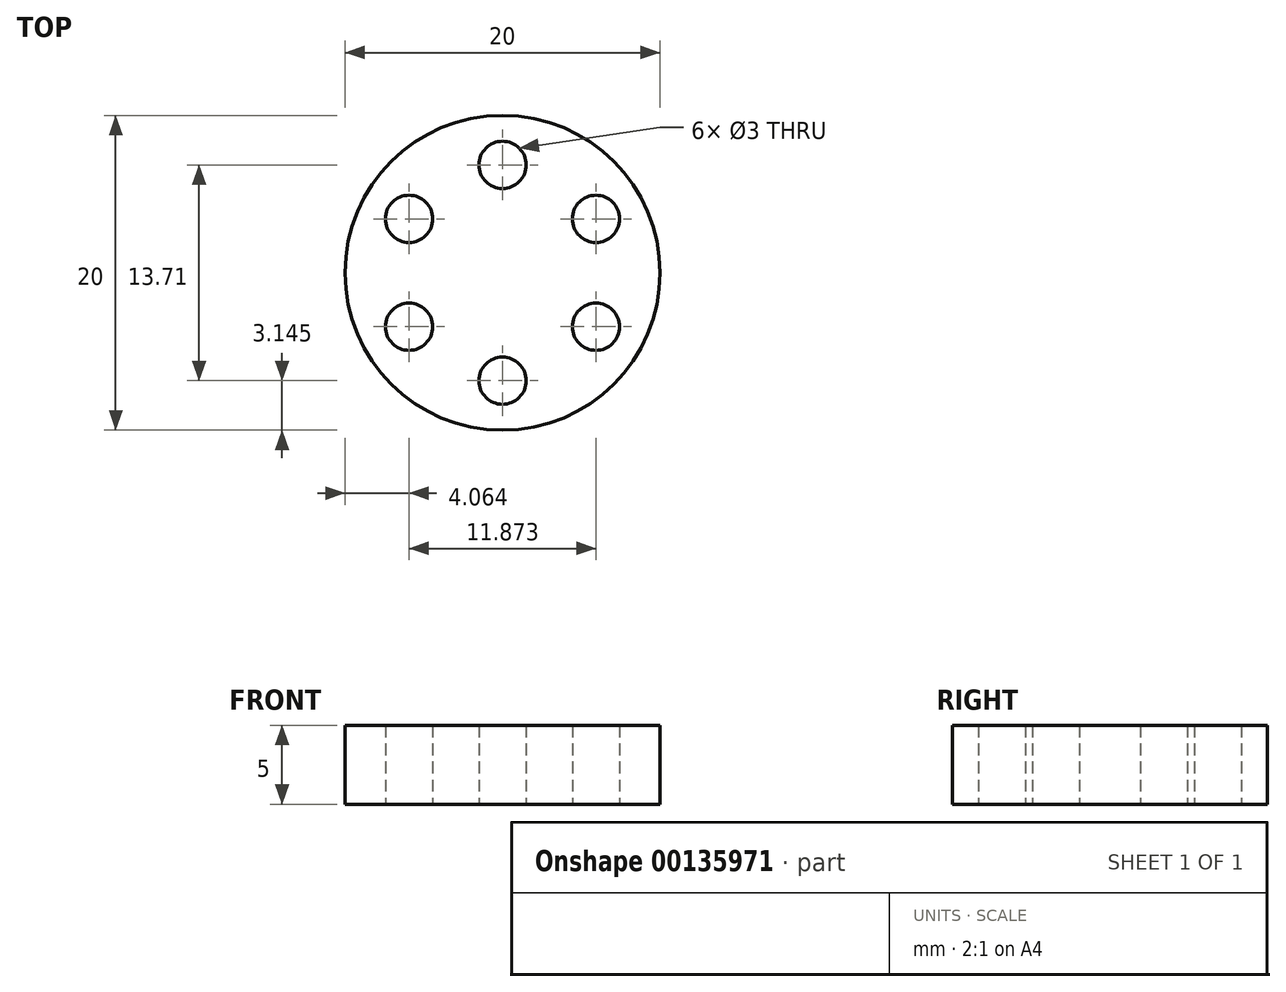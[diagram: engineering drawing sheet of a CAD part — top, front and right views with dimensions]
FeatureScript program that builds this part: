
annotation { "Feature Type Name" : "Feature", "Feature Type Description" : "" }
export const myFeature = defineFeature(function(context is Context, id is Id, definition is map)
    precondition{}
    {
        {
            var Q0;
            Q0=qCreatedBy(makeId("Top.planeOp"),FACE);
            var sketch = newSketch(context, id + "F0", { "sketchPlane" : qUnion([Q0])});
            skCircle(sketch, "E0", {"center": v(0, 0) * mm, "radius": 10 * mm});
            skCircle(sketch, "E1", {"center": v(0, 6.85) * mm, "radius": 1.5 * mm});
            skCircle(sketch, "E2.1.0", {"center": v(5.94, 3.43) * mm, "radius": 1.5 * mm});
            skCircle(sketch, "E2.2.0", {"center": v(5.94, -3.43) * mm, "radius": 1.5 * mm});
            skCircle(sketch, "E2.3.0", {"center": v(0, -6.85) * mm, "radius": 1.5 * mm});
            skCircle(sketch, "E2.4.0", {"center": v(-5.94, -3.43) * mm, "radius": 1.5 * mm});
            skCircle(sketch, "E2.5.0", {"center": v(-5.94, 3.43) * mm, "radius": 1.5 * mm});
            skLineSegment(sketch, "E2.anchor1", {"start": v(0, 0) * mm, "end": v(0, 6.85) * mm, "construction": true});
            skLineSegment(sketch, "E2.anchor2", {"start": v(0, 0) * mm, "end": v(-5.94, 3.43) * mm, "construction": true});
            skSolve(sketch);
        }
        {
            var Q0;
            Q0=makeQuery(id+"F0.imprint","IMPRINT",FACE,{"disambiguationData":[TD([[makeQuery(id+"F0.imprint","IMPRINT",EDGE,{"derivedFrom":sQuery(id+"F0.wireOp",EDGE,"E0")}),1.0]])]});
            extrude(context, id + "F1", {"entities" : qUnion([Q0]), "depth" : 5 * mm});
        }
    });
